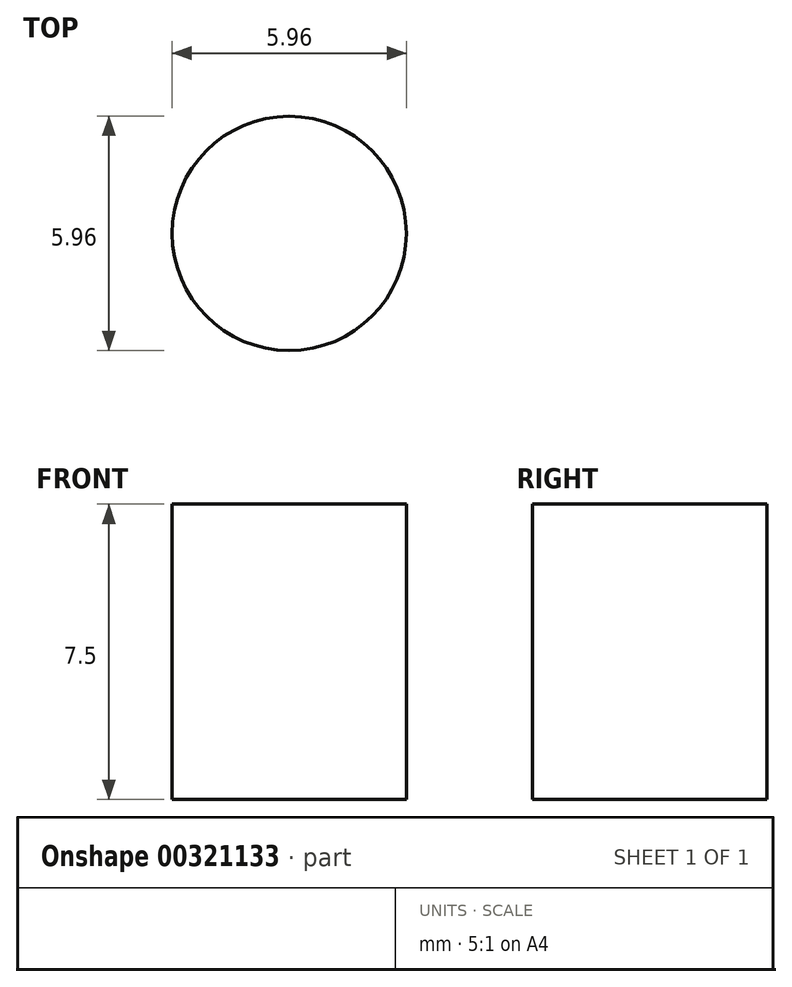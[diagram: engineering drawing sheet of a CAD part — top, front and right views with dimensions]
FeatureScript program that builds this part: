
annotation { "Feature Type Name" : "Feature", "Feature Type Description" : "" }
export const myFeature = defineFeature(function(context is Context, id is Id, definition is map)
    precondition{}
    {
        {
            var Q0;
            Q0=qCreatedBy(makeId("Top.planeOp"),FACE);
            var sketch = newSketch(context, id + "F0", { "sketchPlane" : qUnion([Q0])});
            skCircle(sketch, "E0", {"center": v(0, 0) * mm, "radius": 8 * mm});
            skCircle(sketch, "E1", {"center": v(0, 0) * mm, "radius": 2.98 * mm});
            skSolve(sketch);
        }
        {
            var Q0;
            Q0=sQuery(id+"F0.wireOp",EDGE,"E1");
            extrude(context, id + "F1", {"bodyType" : ToolBodyType.SURFACE, "surfaceEntities" : qUnion([Q0]), "depth" : 7.5 * mm});
        }
    });
